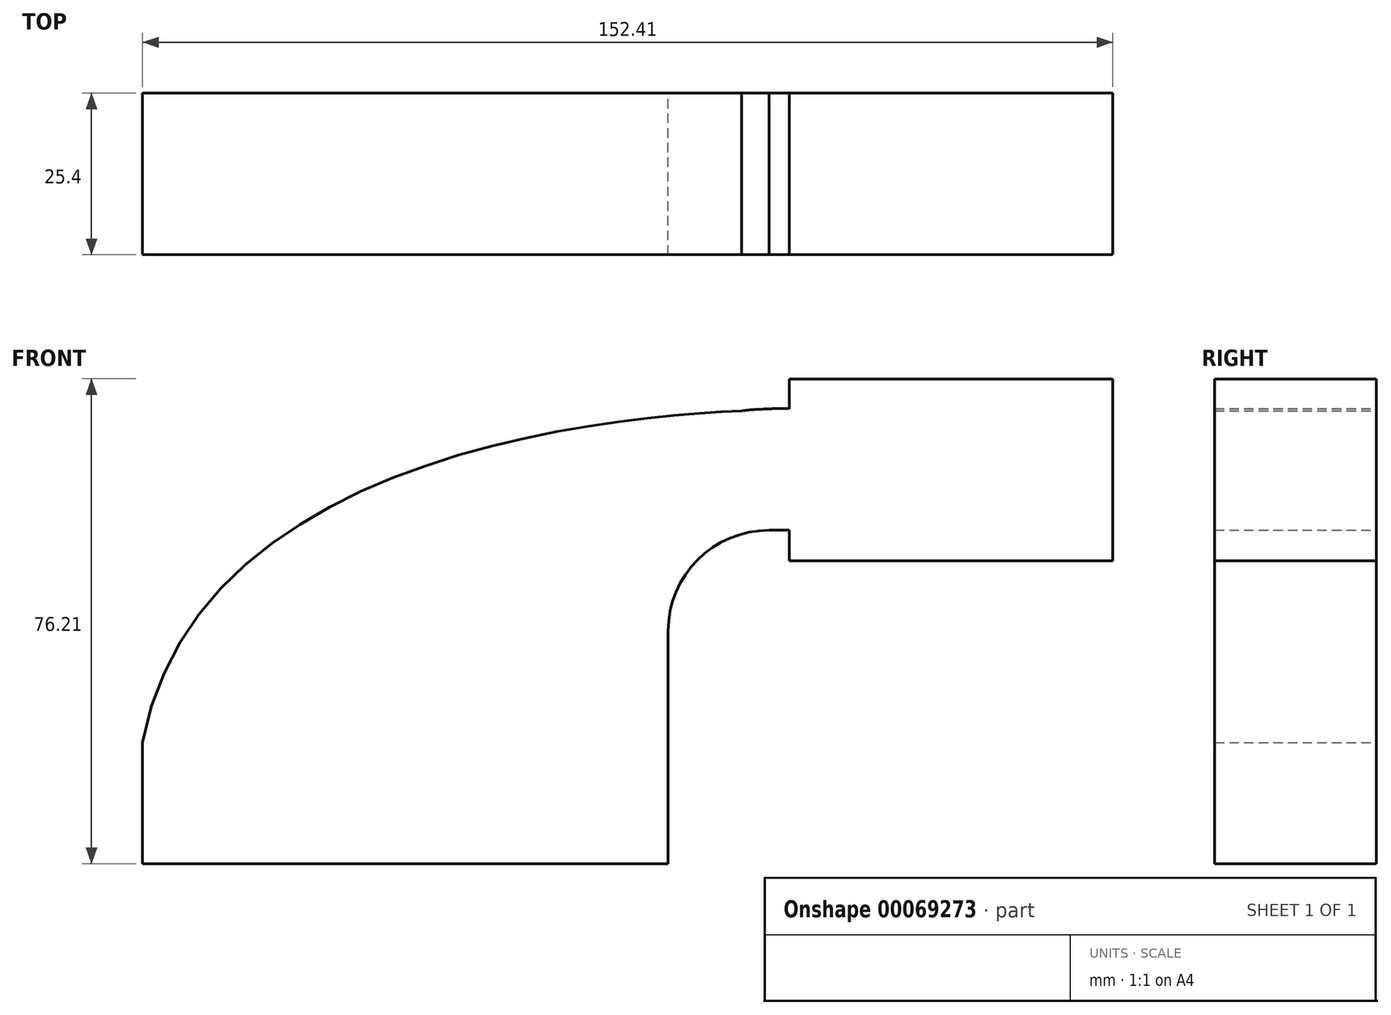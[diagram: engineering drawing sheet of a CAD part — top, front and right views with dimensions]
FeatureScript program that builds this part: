
annotation { "Feature Type Name" : "Feature", "Feature Type Description" : "" }
export const myFeature = defineFeature(function(context is Context, id is Id, definition is map)
    precondition{}
    {
        {
            var Q0;
            Q0=qCreatedBy(makeId("Front.planeOp"),FACE);
            var sketch = newSketch(context, id + "F0", { "sketchPlane" : qUnion([Q0])});
            skLineSegment(sketch, "E0.rect.bottom", {"start": v(-41.27, -9.53) * mm, "end": v(41.28, -9.53) * mm});
            skLineSegment(sketch, "E0.rect.top", {"start": v(-41.28, 9.53) * mm, "end": v(41.28, 9.53) * mm});
            skLineSegment(sketch, "E0.rect.left", {"start": v(-41.28, -9.53) * mm, "end": v(-41.28, 9.53) * mm});
            skLineSegment(sketch, "E0.rect.right", {"start": v(41.28, -9.53) * mm, "end": v(41.28, 9.53) * mm});
            skPoint(sketch, "E0.rect.middle", {"position": v(0, 0) * mm});
            skLineSegment(sketch, "E1.rect.bottom", {"start": v(111.12, 38.1) * mm, "end": v(60.32, 38.1) * mm});
            skLineSegment(sketch, "E1.rect.top", {"start": v(111.12, 66.68) * mm, "end": v(60.32, 66.67) * mm});
            skLineSegment(sketch, "E1.rect.left", {"start": v(111.12, 38.1) * mm, "end": v(111.12, 66.68) * mm});
            skLineSegment(sketch, "E1.rect.right", {"start": v(60.32, 38.1) * mm, "end": v(60.32, 66.68) * mm});
            skPoint(sketch, "E1.rect.middle", {"position": v(85.72, 52.39) * mm});
            skPoint(sketch, "E2.endSnap0", {"position": v(85.72, 38.1) * mm});
            skLineSegment(sketch, "E3", {"start": v(41.28, 9.53) * mm, "end": v(41.28, 27) * mm});
            skArc(sketch, "E4", {"start": v(41.28, 27) * mm, "mid": v(45.92, 38.23) * mm, "end": v(57.15, 42.88) * mm});
            skLineSegment(sketch, "E5", {"start": v(57.15, 42.88) * mm, "end": v(85.72, 42.88) * mm});
            skLineSegment(sketch, "E6.0", {"start": v(57.15, 61.93) * mm, "end": v(85.72, 61.93) * mm});
            skArc(sketch, "E6.1", {"start": v(22.23, 27) * mm, "mid": v(32.45, 51.7) * mm, "end": v(57.15, 61.93) * mm});
            skLineSegment(sketch, "E6.2", {"start": v(22.23, 9.53) * mm, "end": v(22.23, 27) * mm});
            skFitSpline(sketch, "E7", {"points": [v(-41.28, 9.53) * mm, v(60.32, 61.93) * mm, v(57.15, 61.93) * mm], "startDerivative": vector(35.38, 188.98) * mm, "endDerivative": vector(-32.28, -4.37) * mm});
            skLineSegment(sketch, "E8", {"start": v(22.23, 9.53) * mm, "end": v(41.28, 9.53) * mm});
            skLineSegment(sketch, "E9", {"start": v(85.72, 42.88) * mm, "end": v(85.72, 61.93) * mm});
            skSolve(sketch);
        }
        {
            var Q0;
            Q0 = qSketchRegion(id + "F0", true);
            extrude(context, id + "F1", {"entities" : qUnion([Q0]), "depth" : 25.4 * mm});
        }
    });
